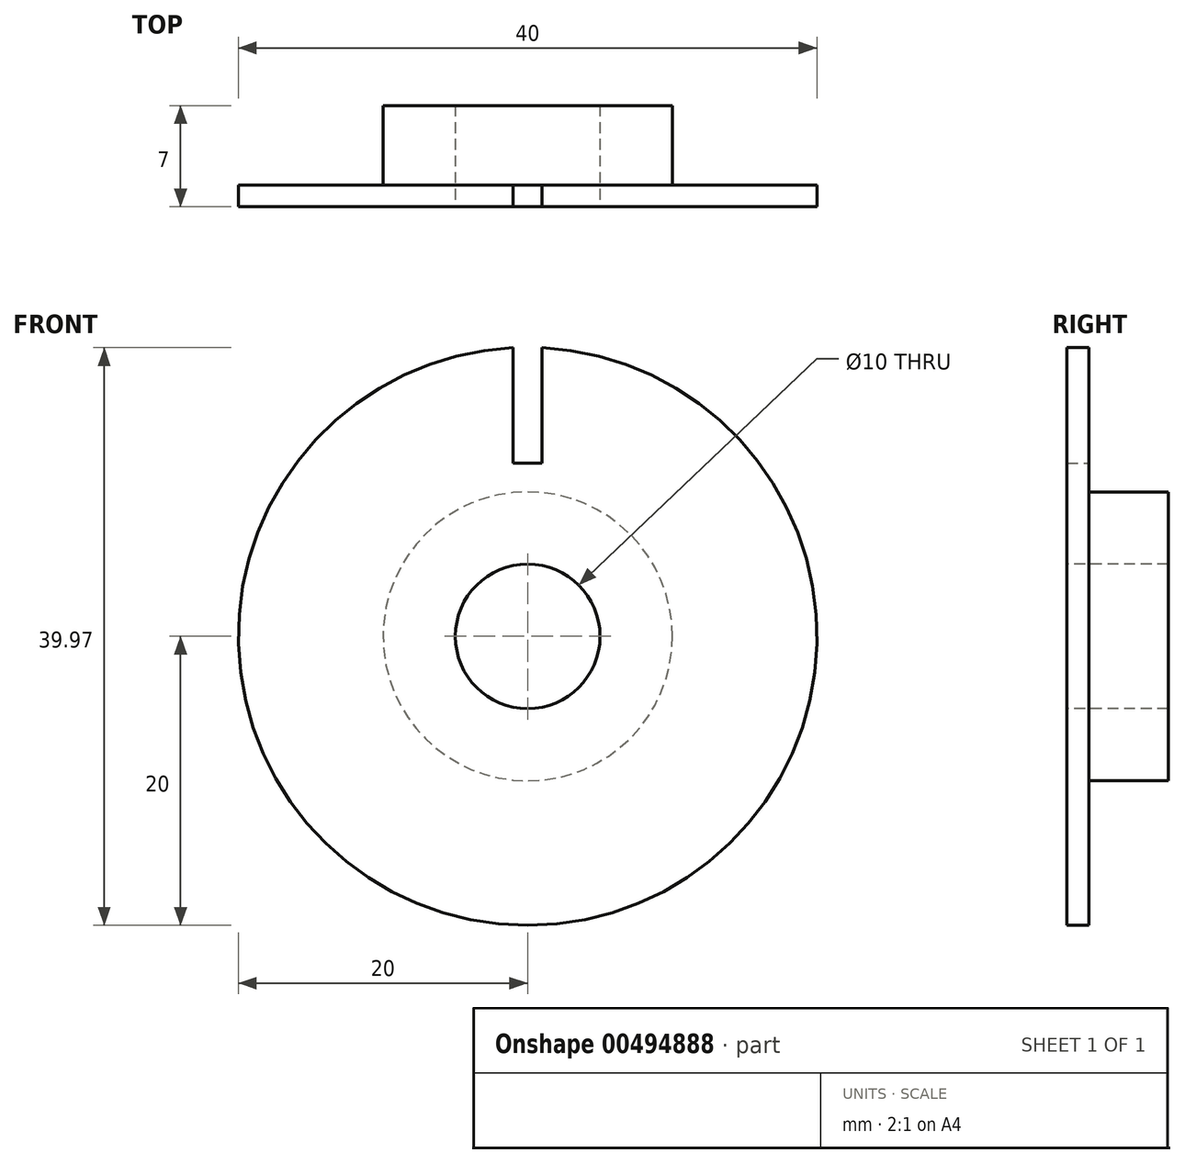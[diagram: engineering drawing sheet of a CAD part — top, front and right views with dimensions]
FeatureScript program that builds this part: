
annotation { "Feature Type Name" : "Feature", "Feature Type Description" : "" }
export const myFeature = defineFeature(function(context is Context, id is Id, definition is map)
    precondition{}
    {
        {
            var Q0;
            Q0=qCreatedBy(makeId("Front.planeOp"),FACE);
            var sketch = newSketch(context, id + "F0", { "sketchPlane" : qUnion([Q0])});
            skCircle(sketch, "E0", {"center": v(0, 0) * mm, "radius": 5 * mm});
            skCircle(sketch, "E1", {"center": v(0, 0) * mm, "radius": 10 * mm});
            skSolve(sketch);
        }
        {
            var Q0;
            Q0=qSketchRegion(id+"F0",true);
            extrude(context, id + "F1", {"entities" : qUnion([Q0]), "oppositeDirection" : true, "depth" : 5.5 * mm});
        }
        {
            var Q0;
            Q0=qCreatedBy(makeId("Front.planeOp"),FACE);
            var sketch = newSketch(context, id + "F2", { "sketchPlane" : qUnion([Q0])});
            skCircle(sketch, "E2", {"center": v(0, 0) * mm, "radius": 20 * mm});
            skCircle(sketch, "E3", {"center": v(0, 0) * mm, "radius": 5 * mm});
            skSolve(sketch);
        }
        {
            var Q0;
            Q0=qSketchRegion(id+"F2",true);
            extrude(context, id + "F3", {"entities" : qUnion([Q0]), "operationType" : NewBodyOperationType.ADD, "depth" : 1.5 * mm});
        }
        {
            var Q0;
            Q0=qCreatedBy(makeId("Front.planeOp"),FACE);
            var sketch = newSketch(context, id + "F4", { "sketchPlane" : qUnion([Q0])});
            skLineSegment(sketch, "E4.bottom", {"start": v(-1, 22) * mm, "end": v(1, 22) * mm});
            skLineSegment(sketch, "E4.top", {"start": v(-1, 12) * mm, "end": v(1, 12) * mm});
            skLineSegment(sketch, "E4.left", {"start": v(-1, 22) * mm, "end": v(-1, 12) * mm});
            skLineSegment(sketch, "E4.right", {"start": v(1, 22) * mm, "end": v(1, 12) * mm});
            skSolve(sketch);
        }
        {
            var Q0;
            Q0=qSketchRegion(id+"F4",true);
            extrude(context, id + "F5", {"entities" : qUnion([Q0]), "operationType" : NewBodyOperationType.REMOVE, "endBound" : BoundingType.THROUGH_ALL, "depth" : 25 * mm});
        }
    });
